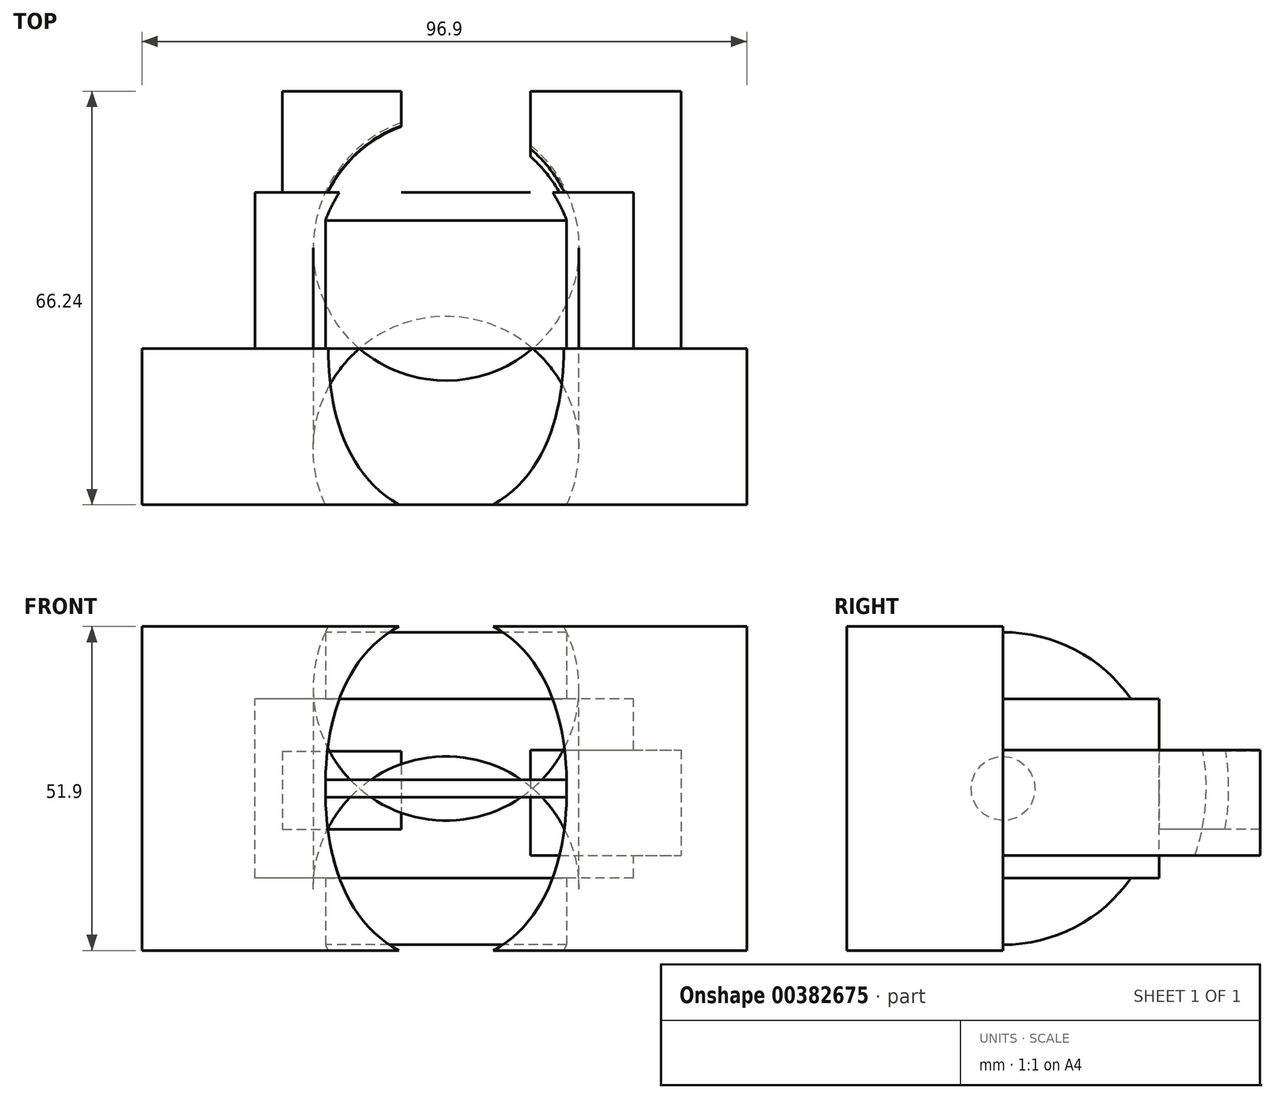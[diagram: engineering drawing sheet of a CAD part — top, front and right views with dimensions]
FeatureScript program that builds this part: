
annotation { "Feature Type Name" : "Feature", "Feature Type Description" : "" }
export const myFeature = defineFeature(function(context is Context, id is Id, definition is map)
    precondition{}
    {
        {
            var Q0;
            Q0=qCreatedBy(makeId("Front.planeOp"),FACE);
            var sketch = newSketch(context, id + "F0", { "sketchPlane" : qUnion([Q0])});
            skLineSegment(sketch, "E0.bottom", {"start": v(-48.45, 25.95) * mm, "end": v(48.45, 25.95) * mm});
            skLineSegment(sketch, "E0.top", {"start": v(-48.45, -25.95) * mm, "end": v(48.45, -25.95) * mm});
            skLineSegment(sketch, "E0.left", {"start": v(-48.45, 25.95) * mm, "end": v(-48.45, -25.95) * mm});
            skLineSegment(sketch, "E0.right", {"start": v(48.45, 25.95) * mm, "end": v(48.45, -25.95) * mm});
            skPoint(sketch, "E0.middle", {"position": v(0, 0) * mm});
            skSolve(sketch);
        }
        {
            var Q0;
            Q0=makeQuery(id+"F0.imprint","IMPRINT",FACE,{"disambiguationData":[TD([[makeQuery(id+"F0.imprint","IMPRINT",EDGE,{"derivedFrom":sQuery(id+"F0.wireOp",EDGE,"E0.bottom")}),-1.0]])]});
            extrude(context, id + "F1", {"entities" : qUnion([Q0]), "depth" : 25 * mm});
        }
        {
            var Q0;
            Q0=qCreatedBy(makeId("Front.planeOp"),FACE);
            var sketch = newSketch(context, id + "F2", { "sketchPlane" : qUnion([Q0])});
            skLineSegment(sketch, "E1.bottom", {"start": v(30.3, -14.33) * mm, "end": v(-30.3, -14.33) * mm});
            skLineSegment(sketch, "E1.top", {"start": v(30.3, 14.33) * mm, "end": v(-30.3, 14.33) * mm});
            skLineSegment(sketch, "E1.left", {"start": v(30.3, -14.33) * mm, "end": v(30.3, 14.33) * mm});
            skLineSegment(sketch, "E1.right", {"start": v(-30.3, -14.33) * mm, "end": v(-30.3, 14.33) * mm});
            skPoint(sketch, "E1.middle", {"position": v(0, 0) * mm});
            skSolve(sketch);
        }
        {
            var Q0;
            Q0 = qSketchRegion(id + "F2", true);
            extrude(context, id + "F3", {"entities" : qUnion([Q0]), "operationType" : NewBodyOperationType.ADD, "oppositeDirection" : true, "depth" : 25 * mm});
        }
        {
            var Q0;
            Q0=makeQuery(id+"F1.opExtrude","CAP_FACE",FACE,{"disambiguationData":[OSD([sQuery(id+"F0.wireOp",EDGE,"E0.bottom"),sQuery(id+"F0.wireOp",EDGE,"E0.top"),sQuery(id+"F0.wireOp",EDGE,"E0.left"),sQuery(id+"F0.wireOp",EDGE,"E0.right")])],"isStart":false});
            var sketch = newSketch(context, id + "F4", { "sketchPlane" : qUnion([Q0])});
            skLineSegment(sketch, "E2.bottom", {"start": v(-25.95, 5.99) * mm, "end": v(-6.9, 5.99) * mm});
            skLineSegment(sketch, "E2.top", {"start": v(-25.95, -6.53) * mm, "end": v(-6.9, -6.53) * mm});
            skLineSegment(sketch, "E2.left", {"start": v(-25.95, 5.99) * mm, "end": v(-25.95, -6.53) * mm});
            skLineSegment(sketch, "E2.right", {"start": v(-6.9, 5.99) * mm, "end": v(-6.9, -6.53) * mm});
            skLineSegment(sketch, "E3.bottom", {"start": v(13.8, 6.17) * mm, "end": v(37.92, 6.17) * mm});
            skLineSegment(sketch, "E3.top", {"start": v(13.8, -10.7) * mm, "end": v(37.92, -10.7) * mm});
            skLineSegment(sketch, "E3.left", {"start": v(13.8, 6.17) * mm, "end": v(13.8, -10.7) * mm});
            skLineSegment(sketch, "E3.right", {"start": v(37.92, 6.17) * mm, "end": v(37.92, -10.7) * mm});
            skSolve(sketch);
        }
        {
            var Q0;
            Q0 = qSketchRegion(id + "F4", true);
            extrude(context, id + "F5", {"entities" : qUnion([Q0]), "operationType" : NewBodyOperationType.ADD, "oppositeDirection" : true, "depth" : 66.2 * mm});
        }
        {
            var Q0;
            Q0=qCreatedBy(makeId("Top.planeOp"),FACE);
            var sketch = newSketch(context, id + "F6", { "sketchPlane" : qUnion([Q0])});
            skLineSegment(sketch, "E4", {"start": v(-67.86, 0) * mm, "end": v(64.23, 0) * mm, "construction": true});
            skArc(sketch, "E5", {"start": v(19.6, 25.04) * mm, "mid": v(0.27, 37.41) * mm, "end": v(-19.05, 25.04) * mm});
            skLineSegment(sketch, "E6", {"start": v(-19.05, 25.04) * mm, "end": v(19.6, 25.04) * mm});
            skSolve(sketch);
        }
        {
            var Q0;
            Q0 = qSketchRegion(id + "F6", true);
            var Q1;
            Q1=sQuery(id+"F6.wireOp",EDGE,"E4");
            revolve(context, id + "F7", {"operationType" : NewBodyOperationType.ADD, "entities" : qUnion([Q0]), "axis" : qUnion([Q1]), "revolveType" : RevolveType.FULL});
        }
    });
